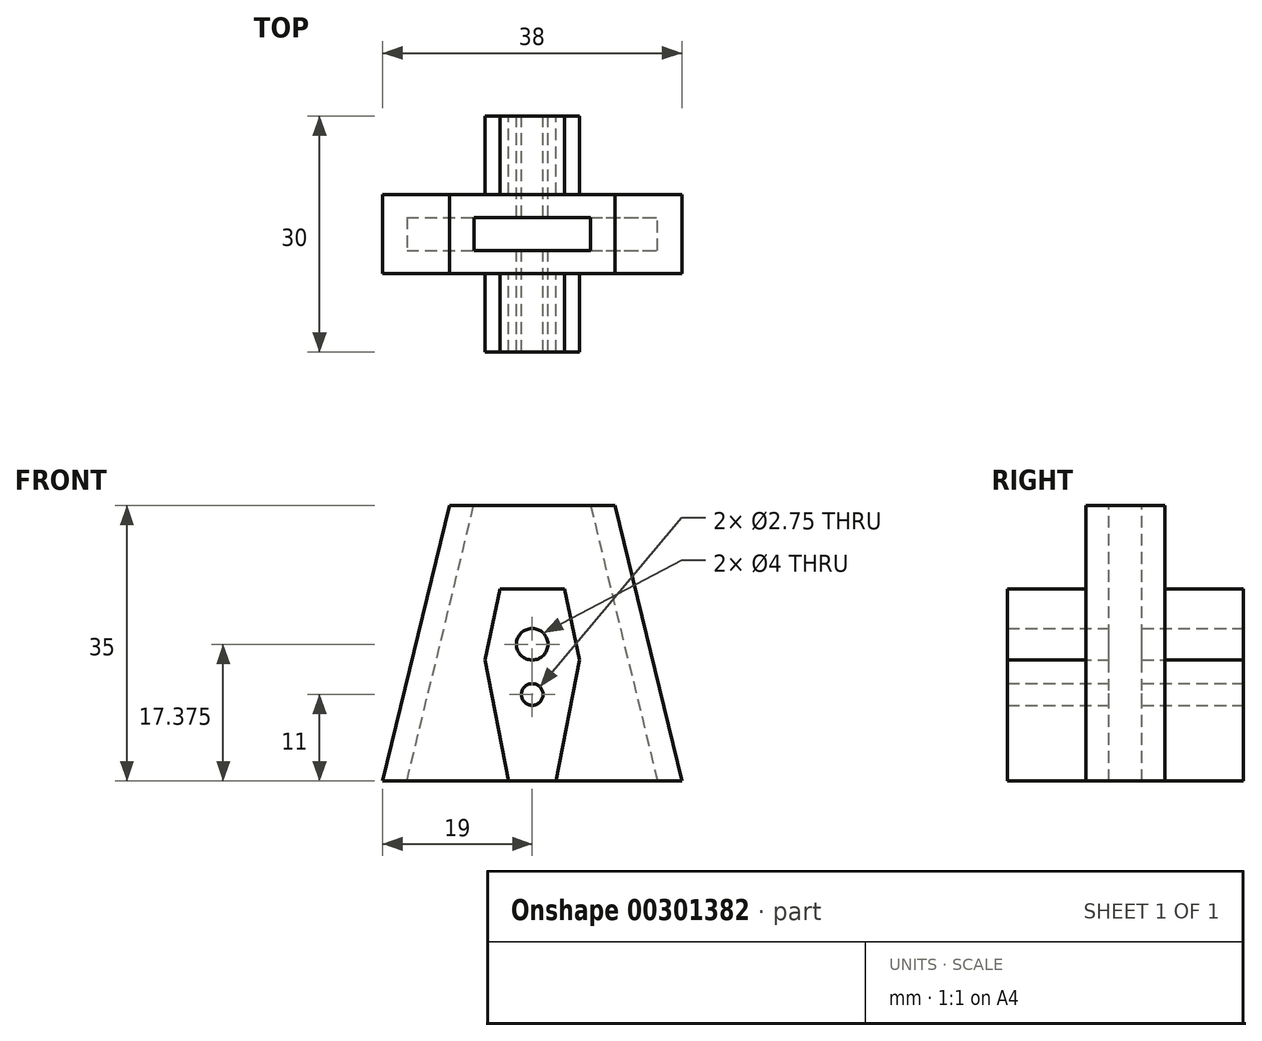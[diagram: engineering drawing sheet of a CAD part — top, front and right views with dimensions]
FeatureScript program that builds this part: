
annotation { "Feature Type Name" : "Feature", "Feature Type Description" : "" }
export const myFeature = defineFeature(function(context is Context, id is Id, definition is map)
    precondition{}
    {
        {
            var Q0;
            Q0=qCreatedBy(makeId("Front.planeOp"),FACE);
            var sketch = newSketch(context, id + "F0", { "sketchPlane" : qUnion([Q0])});
            skLineSegment(sketch, "E0", {"start": v(-19, 0) * mm, "end": v(19, 0) * mm});
            skPoint(sketch, "E1", {"position": v(0, 0) * mm});
            skLineSegment(sketch, "E2", {"start": v(-10.5, 35) * mm, "end": v(10.5, 35) * mm});
            skPoint(sketch, "E3", {"position": v(0, 35) * mm});
            skLineSegment(sketch, "E4", {"start": v(-19, 0) * mm, "end": v(-10.5, 35) * mm});
            skLineSegment(sketch, "E5", {"start": v(10.5, 35) * mm, "end": v(19, 0) * mm});
            skSolve(sketch);
        }
        {
            var Q0;
            Q0=makeQuery(id+"F0.imprint","IMPRINT",FACE,{"disambiguationData":[TD([[makeQuery(id+"F0.imprint","IMPRINT",EDGE,{"derivedFrom":sQuery(id+"F0.wireOp",EDGE,"E0")}),1.0]])]});
            extrude(context, id + "F1", {"entities" : qUnion([Q0]), "endBound" : BoundingType.SYMMETRIC, "depth" : 10 * mm});
        }
        {
            var Q0;
            Q0=qCreatedBy(makeId("Front.planeOp"),FACE);
            var sketch = newSketch(context, id + "F2", { "sketchPlane" : qUnion([Q0])});
            skLineSegment(sketch, "E6.0", {"start": v(-16.08, -0.7) * mm, "end": v(-7.41, 35) * mm});
            skLineSegment(sketch, "E7.0", {"start": v(7.41, 35) * mm, "end": v(16.08, -0.7) * mm});
            skLineSegment(sketch, "E8", {"start": v(-7.41, 35) * mm, "end": v(7.41, 35) * mm});
            skLineSegment(sketch, "E9", {"start": v(-16.08, -0.7) * mm, "end": v(16.08, -0.7) * mm});
            skSolve(sketch);
        }
        {
            var Q0;
            Q0 = qSketchRegion(id + "F2", true);
            extrude(context, id + "F3", {"entities" : qUnion([Q0]), "operationType" : NewBodyOperationType.REMOVE, "endBound" : BoundingType.SYMMETRIC, "depth" : 4.2 * mm});
        }
        {
            var Q0;
            Q0=qCreatedBy(makeId("Front.planeOp"),FACE);
            var sketch = newSketch(context, id + "F4", { "sketchPlane" : qUnion([Q0])});
            skCircle(sketch, "E10", {"center": v(0, 11) * mm, "radius": 1.38 * mm});
            skCircle(sketch, "E11", {"center": v(0, 17.38) * mm, "radius": 2 * mm});
            skLineSegment(sketch, "E12", {"start": v(-4.1, 24.38) * mm, "end": v(4.1, 24.38) * mm});
            skPoint(sketch, "E13", {"position": v(0, 24.38) * mm});
            skLineSegment(sketch, "E14", {"start": v(-3, 0) * mm, "end": v(3, 0) * mm});
            skLineSegment(sketch, "E15", {"start": v(-6, 15.38) * mm, "end": v(-4.1, 24.38) * mm});
            skPoint(sketch, "E16.orphan", {"position": v(-6, 24.38) * mm});
            skLineSegment(sketch, "E17.MirrorCS", {"start": v(6, 15.38) * mm, "end": v(4.1, 24.38) * mm});
            skPoint(sketch, "E18.orphan", {"position": v(6, 24.38) * mm});
            skLineSegment(sketch, "E19", {"start": v(-6, 15.38) * mm, "end": v(-3, 0) * mm});
            skLineSegment(sketch, "E20", {"start": v(6, 15.38) * mm, "end": v(3, 0) * mm});
            skPoint(sketch, "E21.MirrorCS.start.orphan", {"position": v(6, 6.92) * mm});
            skPoint(sketch, "E22.start.orphan", {"position": v(-6, 6.92) * mm});
            skPoint(sketch, "E23.end.orphan", {"position": v(6, 15.38) * mm});
            skPoint(sketch, "E23.start.orphan", {"position": v(0, 15.38) * mm});
            skSolve(sketch);
        }
        {
            var Q0;
            Q0=makeQuery(id+"F4.imprint","IMPRINT",FACE,{"disambiguationData":[TD([[makeQuery(id+"F4.imprint","IMPRINT",EDGE,{"derivedFrom":sQuery(id+"F4.wireOp",EDGE,"E10")}),-1.0]])]});
            extrude(context, id + "F5", {"entities" : qUnion([Q0]), "operationType" : NewBodyOperationType.ADD, "endBound" : BoundingType.SYMMETRIC, "depth" : 30 * mm});
        }
        {
            var Q0;
            Q0=makeQuery(id+"F5.boolean.opBoolean","MERGE",FACE,{"derivedFrom":[makeQuery(id+"F1.opExtrude","SWEPT_FACE",FACE,{"disambiguationData":[OSD([sQuery(id+"F0.wireOp",EDGE,"E0")])]}),makeQuery(id+"F5.opExtrude","SWEPT_FACE",FACE,{"disambiguationData":[OSD([sQuery(id+"F4.wireOp",EDGE,"E14")])]})]});
            var sketch = newSketch(context, id + "F6", { "sketchPlane" : qUnion([Q0])});
            skLineSegment(sketch, "E24.bottom", {"start": v(-6.87, 2.1) * mm, "end": v(6.86, 2.1) * mm});
            skLineSegment(sketch, "E24.top", {"start": v(-6.87, -2.1) * mm, "end": v(6.86, -2.1) * mm});
            skLineSegment(sketch, "E24.left", {"start": v(-6.87, 2.1) * mm, "end": v(-6.87, -2.1) * mm});
            skLineSegment(sketch, "E24.right", {"start": v(6.86, 2.1) * mm, "end": v(6.86, -2.1) * mm});
            skSolve(sketch);
        }
        {
            var Q0;
            {var subQ15=sQuery(id+"F6.wireOp",EDGE,"E24.left");Q0=makeQuery(id+"F6.imprint","IMPRINT",FACE,{"disambiguationData":[TD([[makeQuery(id+"F6.imprint","IMPRINT",EDGE,{"derivedFrom":subQ15}),1.0]])]});}
            var Q1;
            {var subQ1=sQuery(id+"F4.wireOp",EDGE,"E14");var subQ4=sQuery(id+"F2.wireOp",EDGE,"E9");var subQ5=sQuery(id+"F2.wireOp",EDGE,"E8");var subQ6=sQuery(id+"F2.wireOp",EDGE,"E7.0");var subQ7=sQuery(id+"F2.wireOp",EDGE,"E6.0");var subQ9=makeQuery(id+"F3.boolean.opBoolean","COPY",FACE,{"derivedFrom":makeQuery(id+"F3.opExtrude","CAP_FACE",FACE,{"disambiguationData":[OSD([subQ7,subQ6,subQ5,subQ4])],"isStart":true})});var subQ10=sQuery(id+"F4.wireOp",EDGE,"E19");var subQ11=makeQuery(id+"F5.boolean.opBoolean","SPLIT",EDGE,{"disambiguationData":[TD([subQ9])],"derivedFrom":makeQuery(id+"F5.opExtrude","SWEPT_EDGE",EDGE,{"disambiguationData":[OSD([subQ1,subQ10])]})});Q1=makeQuery(id+"F6.imprint","IMPRINT",FACE,{"disambiguationData":[TD([[makeQuery(id+"F6.imprint","IMPRINT",EDGE,{"derivedFrom":subQ11}),1.0]])]});}
            var Q2;
            {var subQ15=sQuery(id+"F6.wireOp",EDGE,"E24.right");Q2=makeQuery(id+"F6.imprint","IMPRINT",FACE,{"disambiguationData":[TD([[makeQuery(id+"F6.imprint","IMPRINT",EDGE,{"derivedFrom":subQ15}),-1.0]])]});}
            extrude(context, id + "F7", {"entities" : qUnion([Q0, Q1, Q2]), "operationType" : NewBodyOperationType.REMOVE, "endBound" : BoundingType.THROUGH_ALL, "oppositeDirection" : true, "depth" : 25 * mm});
        }
        {
            var Q0;
            Q0=makeQuery(id+"F5.boolean.opBoolean","SPLIT",FACE,{"disambiguationData":[TD([makeQuery(id+"F5.opExtrude","SWEPT_FACE",FACE,{"disambiguationData":[OSD([sQuery(id+"F4.wireOp",EDGE,"E11")])]})])],"derivedFrom":makeQuery(id+"F1.opExtrude","CAP_FACE",FACE,{"disambiguationData":[OSD([sQuery(id+"F0.wireOp",EDGE,"E0"),sQuery(id+"F0.wireOp",EDGE,"E2"),sQuery(id+"F0.wireOp",EDGE,"E4"),sQuery(id+"F0.wireOp",EDGE,"E5")])],"isStart":true})});
            var Q1;
            Q1=makeQuery(id+"F5.boolean.opBoolean","SPLIT",FACE,{"disambiguationData":[TD([makeQuery(id+"F5.opExtrude","SWEPT_FACE",FACE,{"disambiguationData":[OSD([sQuery(id+"F4.wireOp",EDGE,"E10")])]})])],"derivedFrom":makeQuery(id+"F1.opExtrude","CAP_FACE",FACE,{"disambiguationData":[OSD([sQuery(id+"F0.wireOp",EDGE,"E0"),sQuery(id+"F0.wireOp",EDGE,"E2"),sQuery(id+"F0.wireOp",EDGE,"E4"),sQuery(id+"F0.wireOp",EDGE,"E5")])],"isStart":true})});
            extrude(context, id + "F8", {"entities" : qUnion([Q0, Q1]), "operationType" : NewBodyOperationType.REMOVE, "endBound" : BoundingType.THROUGH_ALL, "oppositeDirection" : true, "depth" : 25 * mm});
        }
    });
